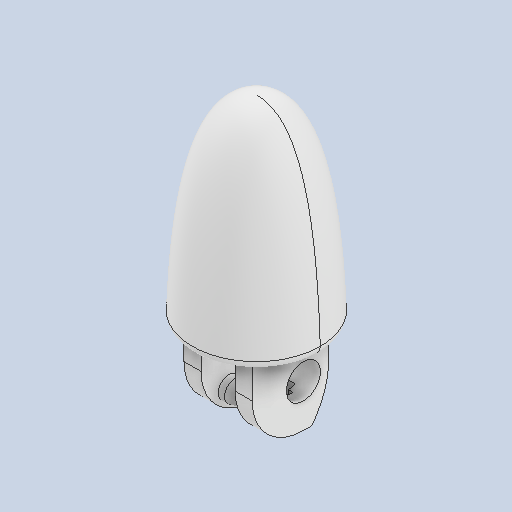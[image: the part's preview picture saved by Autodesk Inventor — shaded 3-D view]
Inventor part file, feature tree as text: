
AUTODESK INVENTOR PART (.ipt)
format: ipt  version: 2022 (Build 260153000, 153)  size: 320,512 bytes
history: native  units: in
note: dims shown in document units (in); Inventor stores cm internally (conversion verified against a paired STEP export)
features: sketch x11, extrude x8, fillet x3, plane x2, hole x2, chamfer x2, revolve x1
ambient origin geometry x8: Origin, YZ Plane, XZ Plane, XY Plane, X Axis, Y Axis, Z Axis, Center Point
bodies: Solid1 (feature_tree)
feature tree (29):
  extrude  "Extrusion1"  TaperAngle=90.0deg  [1 undecoded]
  plane  "Work Plane1"
  revolve  "Revolution1"  [1 undecoded]
  plane  "Work Plane2"
  hole  "Hole1"  [1 undecoded]
  fillet  "Fillet2"  Radius=0.1969in
  fillet  "Fillet3"  Radius=0.0197in
  hole  "Hole2"  [1 undecoded]
  extrude  "Extrusion4"  Depth=0.0492in
  extrude  "Extrusion5"  Depth=0.0098in TaperAngle=45.0deg
  extrude  "Extrusion6"  Depth=0.0098in TaperAngle=45.0deg
  extrude  "Extrusion7"  Depth=0.0394in
  extrude  "Extrusion8"  Depth=0.0344in
  chamfer  "Chamfer1"  Distance=0.0344in
  extrude  "Extrusion9"  [1 undecoded]
  chamfer  "Chamfer2"  [1 undecoded]
  extrude  "Extrusion10"  [1 undecoded]
  fillet  "Fillet5"  [1 undecoded]
  sketch  "Sketch1"  dims[d7=0.3543in d8=0.0in d22=90.0deg]
  sketch  "Sketch5"  dims[d23=0.0394in d24=0.2362in d25=0.1575in d26=0.0787in d27=90.0deg d28=0.7825in d29=0.0in d31=0.0787in]
  sketch  "Sketch6"  dims[d32=0.3937in d33=0.2362in d34=0.1969in]
  sketch  "Sketch7"  dims[d35=0.1575in d36=0.2362in d37=0.1575in d38=0.0787in d39=90.0deg d40=0.595in d41=0.0in d45=0.0197in d46=0.0in]
  sketch  "Sketch8"  dims[d50=0.0197in d51=0.0in d52=0.0197in d53=0.0in]
  sketch  "Sketch9"  dims[d54=0.0197in d55=0.0in d56=0.0492in]
  sketch  "Sketch10"  dims[d57=0.0787in d58=0.0in d59=0.0098in d60=0.0492in d61=45.0deg]
  sketch  "Sketch11"  dims[d62=0.0787in d63=0.0in d64=0.0098in d65=0.0492in d66=45.0deg]
  sketch  "Sketch12"  dims[d68=0.0394in d69=0.0in d70=0.0394in]
  sketch  "Sketch13"  dims[d13=0.0197in d14=0.0344in]
  sketch  "Sketch14"  dims[d15=0.0197in d16=0.0344in]
note: 8 required parameter values undecoded (feature->parameter linkage not recoverable at this tier; creation-order binding heuristic only, values carry confidence <= 0.55)